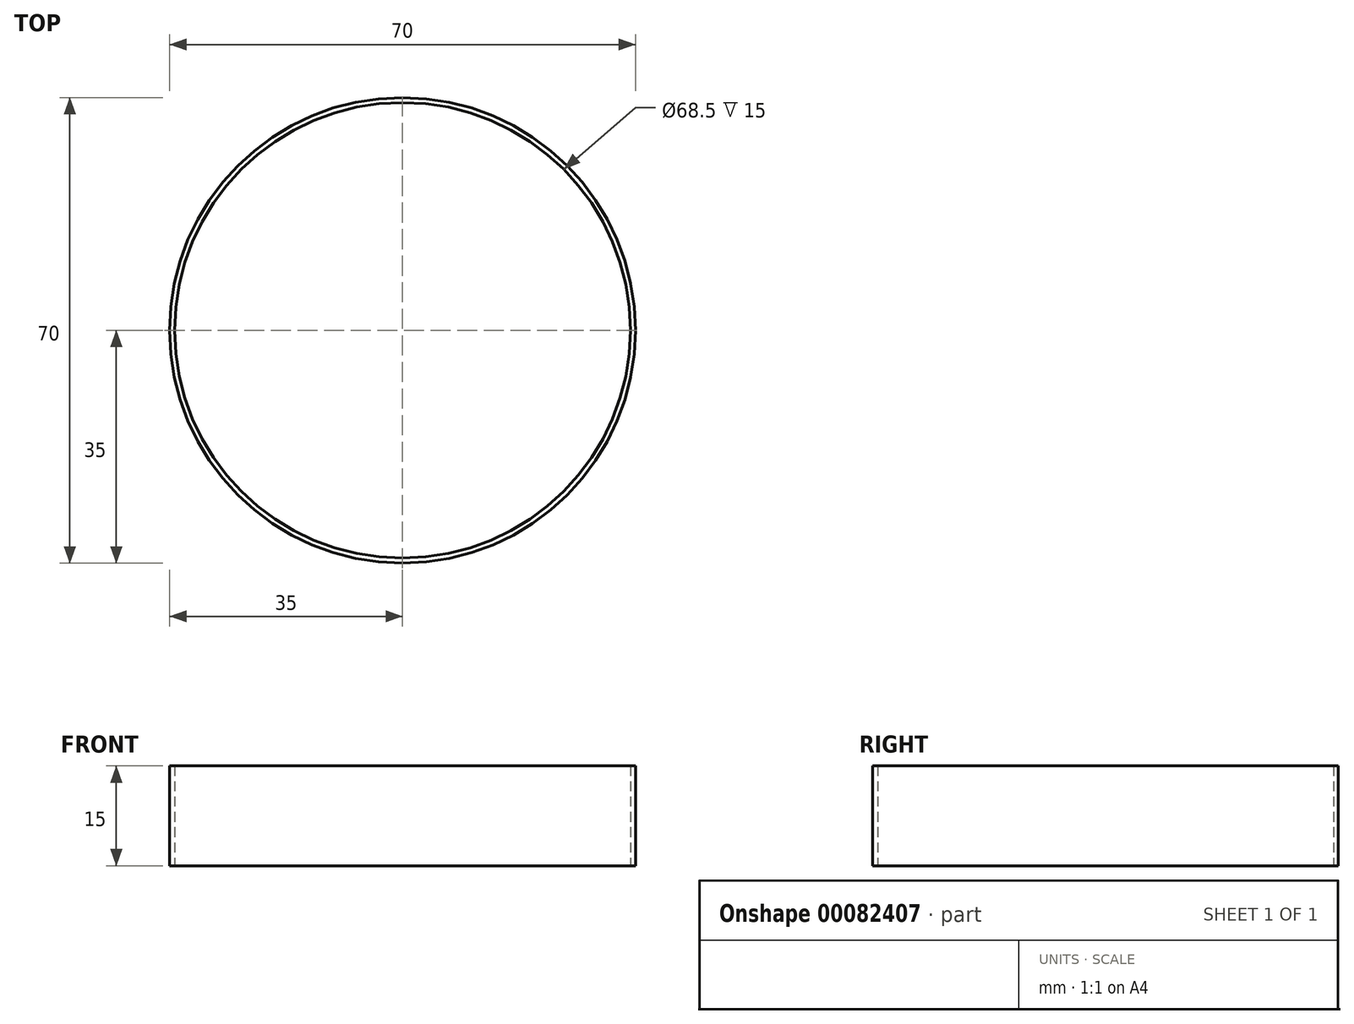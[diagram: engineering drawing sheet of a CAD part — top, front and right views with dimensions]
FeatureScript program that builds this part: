
annotation { "Feature Type Name" : "Feature", "Feature Type Description" : "" }
export const myFeature = defineFeature(function(context is Context, id is Id, definition is map)
    precondition{}
    {
        {
            var Q0;
            Q0=qCreatedBy(makeId("Top.planeOp"),FACE);
            var sketch = newSketch(context, id + "F0", { "sketchPlane" : qUnion([Q0])});
            skCircle(sketch, "E0", {"center": v(0, 0) * mm, "radius": 35 * mm});
            skCircle(sketch, "E1", {"center": v(0, 0) * mm, "radius": 34.25 * mm});
            skSolve(sketch);
        }
        {
            var Q0;
            Q0=makeQuery(id+"F0.imprint","IMPRINT",FACE,{"disambiguationData":[TD([[makeQuery(id+"F0.imprint","IMPRINT",EDGE,{"derivedFrom":sQuery(id+"F0.wireOp",EDGE,"E0")}),1.0]])]});
            extrude(context, id + "F1", {"entities" : qUnion([Q0]), "depth" : 15 * mm});
        }
    });
